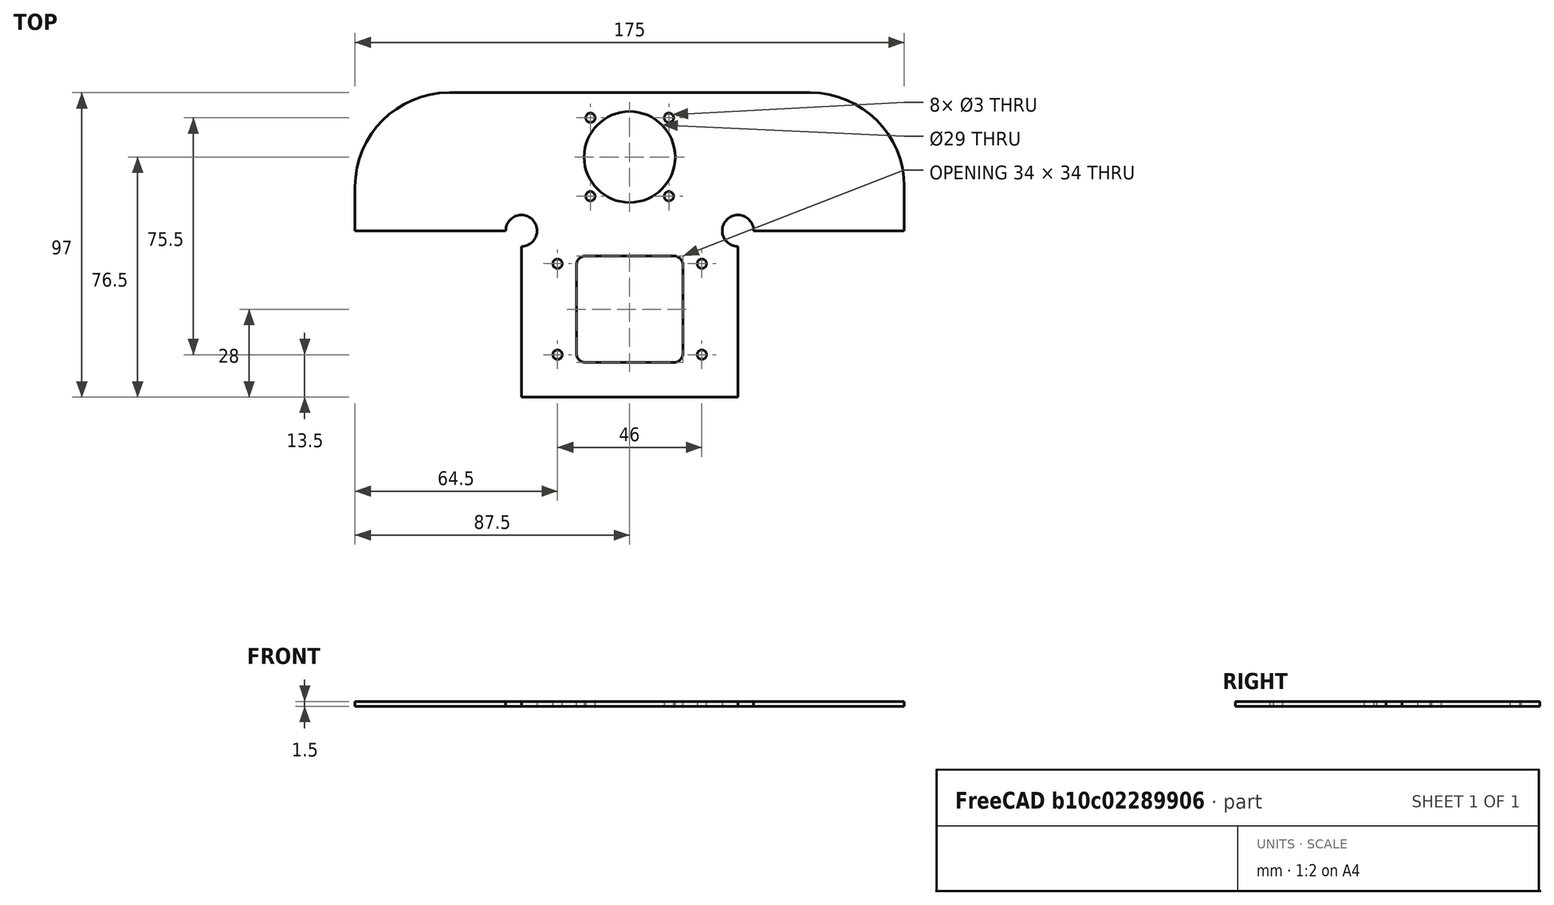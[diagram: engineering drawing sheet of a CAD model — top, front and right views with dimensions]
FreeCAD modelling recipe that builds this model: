
FCSTD DOCUMENT  (FreeCAD 0.19R)
Label: tole_adaptation_extrudeur_tete_mobile_depliée
License: All rights reserved
LicenseURL: http://en.wikipedia.org/wiki/All_rights_reserved
objects: TechDraw::DrawViewPart×2, Sketcher::SketchObject×1, PartDesign::Pad×1, PartDesign::Body×1, TechDraw::DrawSVGTemplate×1, TechDraw::DrawPage×1
note: 4 computed .brp shape members not serialized (recipe doc carries the construction recipe); baked Part::Feature solids carry a one-line shape summary decoded from their .brp

FEATURE [Sketcher::SketchObject] Sketch
  FullyConstrained = false
  MapMode = 5
  Support = -> [XY_Plane]
  sketch-geometry (34):
    g0: LineSegment StartX=-14 StartY=0 StartZ=0 EndX=14 EndY=0 EndZ=0
    g1: LineSegment StartX=17 StartY=-3 StartZ=0 EndX=17 EndY=-31 EndZ=0
    g2: LineSegment StartX=14 StartY=-34 StartZ=0 EndX=-14 EndY=-34 EndZ=0
    g3: LineSegment StartX=-17 StartY=-31 StartZ=0 EndX=-17 EndY=-3 EndZ=0
    g4: ArcOfCircle CenterX=14 CenterY=-3 CenterZ=0 NormalX=0 NormalY=0 NormalZ=1 AngleXU=0 Radius=3 StartAngle=0 EndAngle=1.5708
    g5: ArcOfCircle CenterX=14 CenterY=-31 CenterZ=0 NormalX=0 NormalY=0 NormalZ=1 AngleXU=0 Radius=3 StartAngle=4.71239 EndAngle=6.28319
    g6: ArcOfCircle CenterX=-14 CenterY=-31 CenterZ=0 NormalX=0 NormalY=0 NormalZ=1 AngleXU=0 Radius=3 StartAngle=3.14159 EndAngle=4.71239
    g7: ArcOfCircle CenterX=-14 CenterY=-3 CenterZ=0 NormalX=0 NormalY=0 NormalZ=1 AngleXU=0 Radius=3 StartAngle=1.5708 EndAngle=3.14159
    g8: Circle CenterX=23 CenterY=-2.5 CenterZ=0 NormalX=0 NormalY=0 NormalZ=1 AngleXU=0 Radius=1.5
    g9: Circle CenterX=23 CenterY=-31.5 CenterZ=0 NormalX=0 NormalY=0 NormalZ=1 AngleXU=0 Radius=1.5
    g10: Circle CenterX=-23 CenterY=-2.5 CenterZ=0 NormalX=0 NormalY=0 NormalZ=1 AngleXU=0 Radius=1.5
    g11: Circle CenterX=-23 CenterY=-31.5 CenterZ=0 NormalX=0 NormalY=0 NormalZ=1 AngleXU=0 Radius=1.5
    g12: LineSegment StartX=23 StartY=-2.5 StartZ=0 EndX=23 EndY=-31.5 EndZ=0
    g13: LineSegment StartX=-14 StartY=-3 StartZ=0 EndX=14 EndY=-31 EndZ=0
    g14: LineSegment StartX=0 StartY=-17 StartZ=0 EndX=30.7651 EndY=-17 EndZ=0
    g15: LineSegment StartX=-29.5 StartY=8 StartZ=0 EndX=29.5 EndY=8 EndZ=0
    g16: LineSegment StartX=34.5 StartY=-45 StartZ=0 EndX=-34.5 EndY=-45 EndZ=0
    g17: LineSegment StartX=87.5 StartY=8 StartZ=0 EndX=39.5 EndY=8 EndZ=0
    g18: ArcOfCircle CenterX=34.5 CenterY=8 CenterZ=0 NormalX=0 NormalY=0 NormalZ=1 AngleXU=0 Radius=5 StartAngle=1e-16 EndAngle=4.71239
    g19: ArcOfCircle CenterX=-34.5 CenterY=8 CenterZ=0 NormalX=0 NormalY=0 NormalZ=1 AngleXU=0 Radius=5 StartAngle=4.71239 EndAngle=9.42478
    g20: LineSegment StartX=-87.5 StartY=8 StartZ=0 EndX=-39.5 EndY=8 EndZ=0
    g21: LineSegment StartX=57.5 StartY=52 StartZ=0 EndX=-57.5 EndY=52 EndZ=0
    g22: Circle CenterX=0 CenterY=31.5 CenterZ=0 NormalX=0 NormalY=0 NormalZ=1 AngleXU=0 Radius=14.5
    g23: Circle CenterX=-12.5 CenterY=44 CenterZ=0 NormalX=0 NormalY=0 NormalZ=1 AngleXU=0 Radius=1.5
    g24: Circle CenterX=12.5 CenterY=44 CenterZ=0 NormalX=0 NormalY=0 NormalZ=1 AngleXU=0 Radius=1.5
    g25: Circle CenterX=12.5 CenterY=19 CenterZ=0 NormalX=0 NormalY=0 NormalZ=1 AngleXU=0 Radius=1.5
    g26: Circle CenterX=-12.5 CenterY=19 CenterZ=0 NormalX=0 NormalY=0 NormalZ=1 AngleXU=0 Radius=1.5
    g27: LineSegment StartX=0 StartY=31.5 StartZ=0 EndX=34.5 EndY=31.5 EndZ=0
    g28: ArcOfCircle CenterX=-57.5 CenterY=22 CenterZ=0 NormalX=0 NormalY=0 NormalZ=1 AngleXU=0 Radius=30 StartAngle=1.5708 EndAngle=3.14159
    g29: LineSegment StartX=-87.5 StartY=22 StartZ=0 EndX=-87.5 EndY=8 EndZ=0
    g30: ArcOfCircle CenterX=57.5 CenterY=22 CenterZ=0 NormalX=0 NormalY=0 NormalZ=1 AngleXU=0 Radius=30 StartAngle=0 EndAngle=1.5708
    g31: LineSegment StartX=87.5 StartY=22 StartZ=0 EndX=87.5 EndY=8 EndZ=0
    g32: LineSegment StartX=34.5 StartY=3 StartZ=0 EndX=34.5 EndY=-45 EndZ=0
    g33: LineSegment StartX=-34.5 StartY=3 StartZ=0 EndX=-34.5 EndY=-45 EndZ=0
  constraints (87):
    c: Horizontal(g2)
    c: Vertical(g1)
    c: Vertical(g3)
    c: Tangent(g0,g4) = 1.5708
    c: Tangent(g1,g4) = 1.5708
    c: Tangent(g1,g5) = 1.5708
    c: Tangent(g2,g5) = 1.5708
    c: Tangent(g2,g6) = 1.5708
    c: Tangent(g3,g6) = 1.5708
    c: Tangent(g3,g7) = 1.5708
    c: Tangent(g0,g7) = 1.5708
    c: Equal(g7,g4)
    c: Equal(g4,g5)
    c: Equal(g5,g6)
    c: Symmetric(g0,g0,g-2)
    c: DistanceX(g3,g1) = 34
    c: Radius(g7) = 3
    c: DistanceY(g2,g0) = 34
    c: PointOnObject(g0,g-1)
    c: Equal(g11,g10)
    c: Equal(g10,g8)
    c: Equal(g8,g9)
    c: Symmetric(g10,g8,g-2)
    c: Symmetric(g9,g11,g-2)
    c: DistanceY(g9,g8) = 29
    c: Coincident(g12,g8)
    c: Coincident(g12,g9)
    c: Vertical(g12)
    c: DistanceX(g10,g8) = 46
    c: Coincident(g13,g7)
    c: Coincident(g13,g5)
    c: PointOnObject(g14,g13)
    c: PointOnObject(g14,g-2)
    c: Symmetric(g8,g9,g14)
    c: Radius(g8) = 1.5
    c: Horizontal(g16)
    c: DistanceY(g0,g15) = 8
    c: Symmetric(g15,g15,g-2)
    c: Horizontal(g17)
    c: PointOnObject(g15,g18)
    c: PointOnObject(g18,g17)
    c: PointOnObject(g15,g17)
    c: PointOnObject(g15,g19)
    c: PointOnObject(g19,g15)
    c: Horizontal(g20)
    c: DistanceX(g19,g18) = 69
    c: Radius(g19) = 5
    c: Equal(g18,g19)
    c: Horizontal(g21)
    c: Symmetric(g17,g20,g-2)
    c: DistanceX(g18,g17) = 53
    c: DistanceY(g18,g21) = 44
    c: PointOnObject(g22,g-2)
    c: Equal(g26,g23)
    c: Equal(g23,g24)
    c: Equal(g24,g25)
    c: Symmetric(g23,g24,g-2)
    c: Symmetric(g26,g25,g-2)
    c: Coincident(g27,g22)
    c: Horizontal(g27)
    c: Symmetric(g24,g25,g27)
    c: Radius(g24) = 1.5
    c: Radius(g22) = 14.5
    c: DistanceX(g23,g24) = 25
    c: DistanceY(g26,g23) = 25
    c: DistanceY(g24,g21) = 8
    c: Coincident(g29,g20)
    c: Vertical(g29)
    c: Tangent(g29,g28) = -1.5708
    c: Tangent(g28,g21) = -1.5708
    c: Radius(g28) = 30
    c: Vertical(g31)
    c: Tangent(g31,g30) = 1.5708
    c: Radius(g30) = 30
    c: Tangent(g21,g30) = -1.5708
    c: Coincident(g31,g17)
    c: Vertical(g32)
    c: Vertical(g33)
    c: Coincident(g16,g33)
    c: Coincident(g16,g32)
    c: Coincident(g19,g33)
    c: Coincident(g19,g20)
    c: PointOnObject(g19,g33)
    c: Coincident(g18,g32)
    c: Coincident(g17,g18)
    c: PointOnObject(g18,g32)
    c: DistanceY(g16,g18) = 53
FEATURE [PartDesign::Pad] Pad
  Direction = (1,1,1)
  Length = 1.5
  Length2 = 100
  Profile = -> Sketch
  Type = 0
FEATURE [PartDesign::Body] Body
  Group = -> [Sketch,Pad]
  Origin = -> Origin
  Tip = -> Pad
FEATURE [TechDraw::DrawSVGTemplate] Template
  EditableTexts = Designed_by_Name=JC Carré; Drawing_number=2/2; FC-Date=23/06/2021; FC-SC=1:1; FC-SH=2/2; FC-Title=équerre adaptation extrudeur
  Height = 210
  Orientation = 1
  Width = 297
FEATURE [TechDraw::DrawViewPart] View
  CoarseView = false
  Direction = (0,0,1)
  Focus = 100
  HardHidden = false
  IsoCount = 0
  IsoHidden = false
  IsoVisible = false
  LockPosition = false
  Perspective = false
  Rotation = 0
  ScaleType = 0
  SeamHidden = false
  SeamVisible = true
  SmoothHidden = false
  SmoothVisible = true
  Source = -> [Body]
  X = 62.6333
  XDirection = (0,-1,0)
  Y = 106.4
FEATURE [TechDraw::DrawViewPart] View001
  CoarseView = false
  Direction = (0,0,1)
  Focus = 100
  HardHidden = false
  IsoCount = 0
  IsoHidden = false
  IsoVisible = false
  LockPosition = false
  Perspective = false
  Rotation = 0
  ScaleType = 0
  SeamHidden = false
  SeamVisible = true
  SmoothHidden = false
  SmoothVisible = true
  Source = -> [Body]
  X = 194.7
  XDirection = (1,0,0)
  Y = 146.067
FEATURE [TechDraw::DrawPage] Page
  KeepUpdated = true
  NextBalloonIndex = 1
  ProjectionType = 0
  Template = -> Template
  Views = -> [View,View001]
